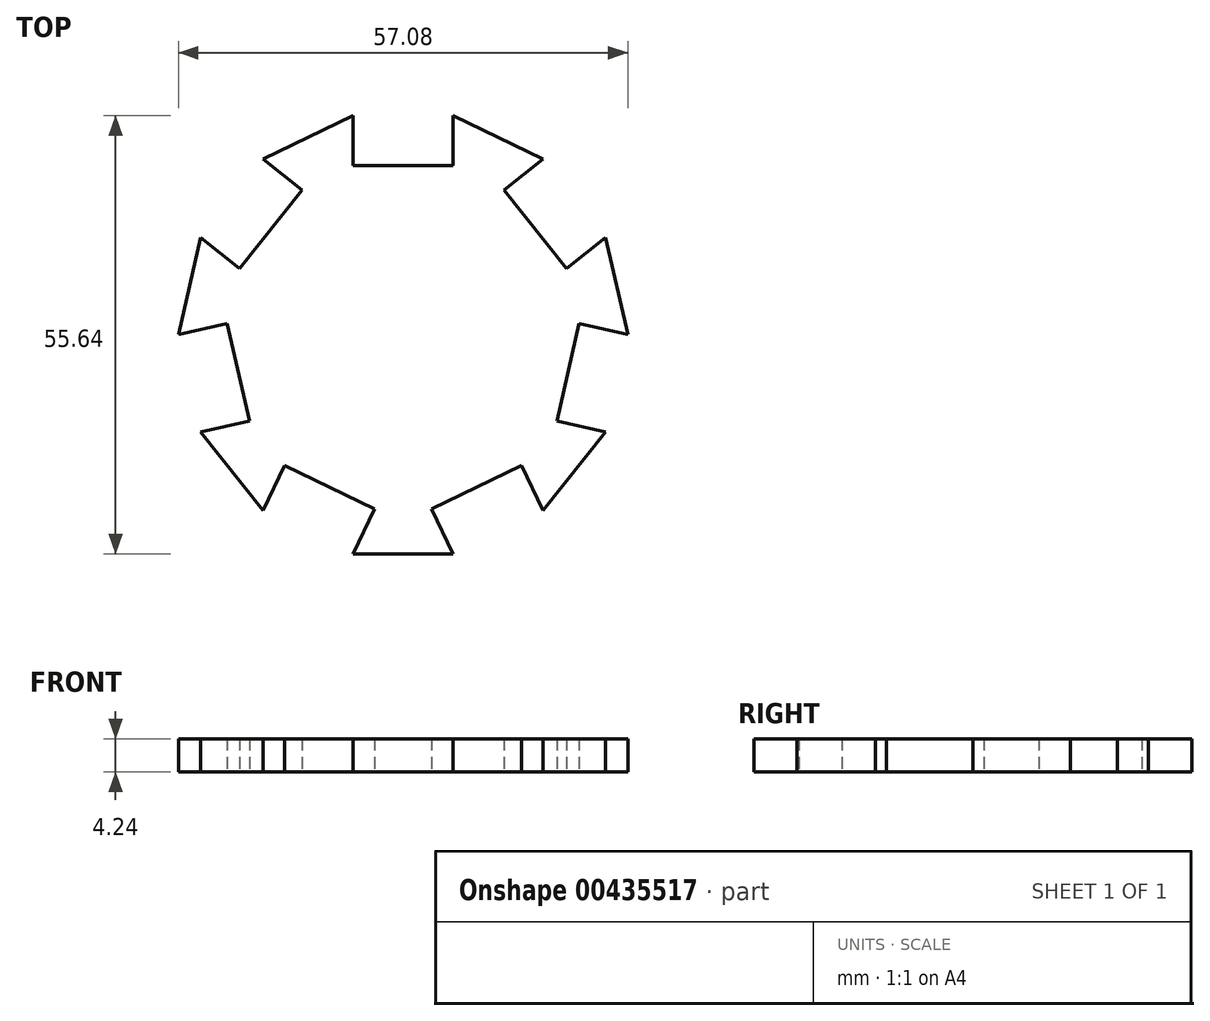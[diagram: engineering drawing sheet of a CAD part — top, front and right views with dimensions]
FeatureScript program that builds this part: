
annotation { "Feature Type Name" : "Feature", "Feature Type Description" : "" }
export const myFeature = defineFeature(function(context is Context, id is Id, definition is map)
    precondition{}
    {
        {
            var Q0;
            Q0=qCreatedBy(makeId("Top.planeOp"),FACE);
            var sketch = newSketch(context, id + "F0", { "sketchPlane" : qUnion([Q0])});
            skCircle(sketch, "E0.cCircle", {"center": v(0, 0) * mm, "radius": 27.82 * mm, "construction": true});
            skLineSegment(sketch, "E0.0", {"start": v(-6.35, 27.82) * mm, "end": v(6.35, 27.82) * mm});
            skLineSegment(sketch, "E0.1", {"start": v(6.35, 27.82) * mm, "end": v(17.8, 22.31) * mm});
            skLineSegment(sketch, "E0.2", {"start": v(17.8, 22.31) * mm, "end": v(25.71, 12.38) * mm});
            skLineSegment(sketch, "E0.3", {"start": v(25.71, 12.38) * mm, "end": v(28.54, 0) * mm});
            skLineSegment(sketch, "E0.4", {"start": v(28.54, 0) * mm, "end": v(25.71, -12.38) * mm});
            skLineSegment(sketch, "E0.5", {"start": v(25.71, -12.38) * mm, "end": v(17.8, -22.31) * mm});
            skLineSegment(sketch, "E0.6", {"start": v(17.8, -22.31) * mm, "end": v(6.35, -27.82) * mm});
            skLineSegment(sketch, "E0.7", {"start": v(6.35, -27.82) * mm, "end": v(-6.35, -27.82) * mm});
            skLineSegment(sketch, "E0.8", {"start": v(-6.35, -27.82) * mm, "end": v(-17.8, -22.31) * mm});
            skLineSegment(sketch, "E0.9", {"start": v(-17.8, -22.31) * mm, "end": v(-25.71, -12.38) * mm});
            skLineSegment(sketch, "E0.10", {"start": v(-25.71, -12.38) * mm, "end": v(-28.54, 0) * mm});
            skLineSegment(sketch, "E0.11", {"start": v(-28.54, 0) * mm, "end": v(-25.71, 12.38) * mm});
            skLineSegment(sketch, "E0.12", {"start": v(-25.71, 12.38) * mm, "end": v(-17.8, 22.31) * mm});
            skLineSegment(sketch, "E0.13", {"start": v(-17.8, 22.31) * mm, "end": v(-6.35, 27.82) * mm});
            skPoint(sketch, "E0.0.midPoint", {"position": v(0, 27.82) * mm});
            skLineSegment(sketch, "E1.rect.bottom", {"start": v(-6.35, 34.17) * mm, "end": v(6.35, 34.17) * mm});
            skLineSegment(sketch, "E1.rect.top", {"start": v(-6.35, 21.47) * mm, "end": v(6.35, 21.47) * mm});
            skLineSegment(sketch, "E1.rect.left", {"start": v(-6.35, 34.17) * mm, "end": v(-6.35, 21.47) * mm});
            skLineSegment(sketch, "E1.rect.right", {"start": v(6.35, 34.17) * mm, "end": v(6.35, 21.47) * mm});
            skLineSegment(sketch, "E2", {"start": v(-22.76, 26.27) * mm, "end": v(-12.83, 18.35) * mm});
            skLineSegment(sketch, "E3", {"start": v(-12.83, 18.35) * mm, "end": v(-20.75, 8.42) * mm});
            skLineSegment(sketch, "E4", {"start": v(-20.75, 8.42) * mm, "end": v(-30.68, 16.34) * mm});
            skLineSegment(sketch, "E5", {"start": v(-30.68, 16.34) * mm, "end": v(-22.76, 26.27) * mm});
            skLineSegment(sketch, "E6", {"start": v(-34.73, -1.41) * mm, "end": v(-22.35, 1.41) * mm});
            skLineSegment(sketch, "E7", {"start": v(-31.9, -13.8) * mm, "end": v(-34.73, -1.41) * mm});
            skLineSegment(sketch, "E8", {"start": v(-19.52, -10.97) * mm, "end": v(-31.9, -13.8) * mm});
            skLineSegment(sketch, "E9", {"start": v(-19.52, -10.97) * mm, "end": v(-22.35, 1.41) * mm});
            skLineSegment(sketch, "E10", {"start": v(-15.04, -16.59) * mm, "end": v(-20.55, -28.03) * mm});
            skLineSegment(sketch, "E11", {"start": v(-20.55, -28.03) * mm, "end": v(-9.1, -33.54) * mm});
            skLineSegment(sketch, "E12", {"start": v(-9.1, -33.54) * mm, "end": v(-3.6, -22.1) * mm});
            skLineSegment(sketch, "E13", {"start": v(-3.6, -22.1) * mm, "end": v(-15.04, -16.59) * mm});
            skLineSegment(sketch, "E14.MirrorCS", {"start": v(12.83, 18.35) * mm, "end": v(20.75, 8.42) * mm});
            skLineSegment(sketch, "E15.MirrorCS", {"start": v(22.76, 26.27) * mm, "end": v(12.83, 18.35) * mm});
            skLineSegment(sketch, "E16.MirrorCS", {"start": v(30.68, 16.34) * mm, "end": v(22.76, 26.27) * mm});
            skLineSegment(sketch, "E17.MirrorCS", {"start": v(20.75, 8.42) * mm, "end": v(30.68, 16.34) * mm});
            skLineSegment(sketch, "E18.MirrorCS", {"start": v(34.73, -1.41) * mm, "end": v(22.35, 1.41) * mm});
            skLineSegment(sketch, "E19.MirrorCS", {"start": v(19.52, -10.97) * mm, "end": v(22.35, 1.41) * mm});
            skLineSegment(sketch, "E20.MirrorCS", {"start": v(31.9, -13.8) * mm, "end": v(34.73, -1.41) * mm});
            skLineSegment(sketch, "E21.MirrorCS", {"start": v(19.52, -10.97) * mm, "end": v(31.9, -13.8) * mm});
            skLineSegment(sketch, "E22.MirrorCS", {"start": v(3.6, -22.1) * mm, "end": v(15.04, -16.59) * mm});
            skLineSegment(sketch, "E23.MirrorCS", {"start": v(20.55, -28.03) * mm, "end": v(9.1, -33.54) * mm});
            skLineSegment(sketch, "E24.MirrorCS", {"start": v(15.04, -16.59) * mm, "end": v(20.55, -28.03) * mm});
            skLineSegment(sketch, "E25.MirrorCS", {"start": v(9.1, -33.54) * mm, "end": v(3.6, -22.1) * mm});
            skSolve(sketch);
        }
        {
            var Q0;
            {var subQ2=sQuery(id+"F0.wireOp",EDGE,"E0.1");Q0=makeQuery(id+"F0.imprint","IMPRINT",FACE,{"disambiguationData":[TD([[makeQuery(id+"F0.imprint","IMPRINT",EDGE,{"derivedFrom":subQ2}),-1.0]])]});}
            extrude(context, id + "F1", {"entities" : qUnion([Q0]), "endBound" : BoundingType.SYMMETRIC, "depth" : 4.23 * mm});
        }
    });
